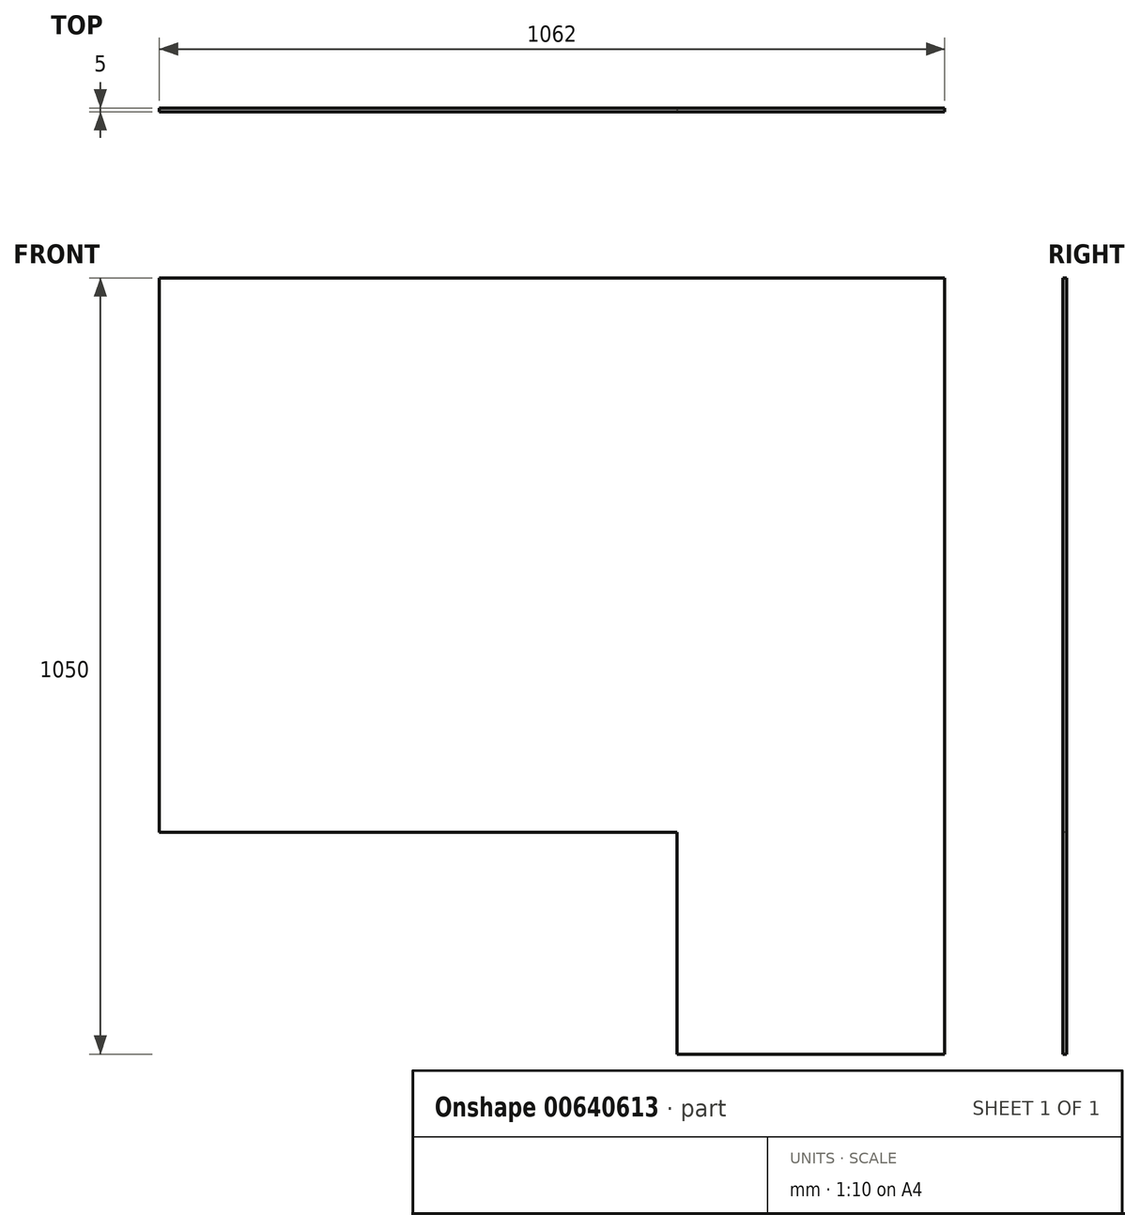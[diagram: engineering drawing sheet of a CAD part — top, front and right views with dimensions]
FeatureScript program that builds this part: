
annotation { "Feature Type Name" : "Feature", "Feature Type Description" : "" }
export const myFeature = defineFeature(function(context is Context, id is Id, definition is map)
    precondition{}
    {
        {
            var Q0;
            Q0=qCreatedBy(makeId("Front.planeOp"),FACE);
            var sketch = newSketch(context, id + "F0", { "sketchPlane" : qUnion([Q0])});
            skLineSegment(sketch, "E0.bottom", {"start": v(0, 0) * mm, "end": v(-362, 0) * mm});
            skLineSegment(sketch, "E0.top", {"start": v(0, 1050) * mm, "end": v(-1062, 1050) * mm});
            skLineSegment(sketch, "E0.left", {"start": v(0, 0) * mm, "end": v(0, 1050) * mm});
            skLineSegment(sketch, "E0.right", {"start": v(-362, 0) * mm, "end": v(-362, 300) * mm});
            skLineSegment(sketch, "E1.top", {"start": v(-362, 300) * mm, "end": v(-1062, 300) * mm});
            skLineSegment(sketch, "E1.right", {"start": v(-1062, 1050) * mm, "end": v(-1062, 300) * mm});
            skSolve(sketch);
        }
        {
            var Q0;
            Q0 = qSketchRegion(id + "F0", true);
            extrude(context, id + "F1", {"entities" : qUnion([Q0]), "oppositeDirection" : true, "depth" : 5 * mm, "offsetDistance" : 25 * mm});
        }
    });
